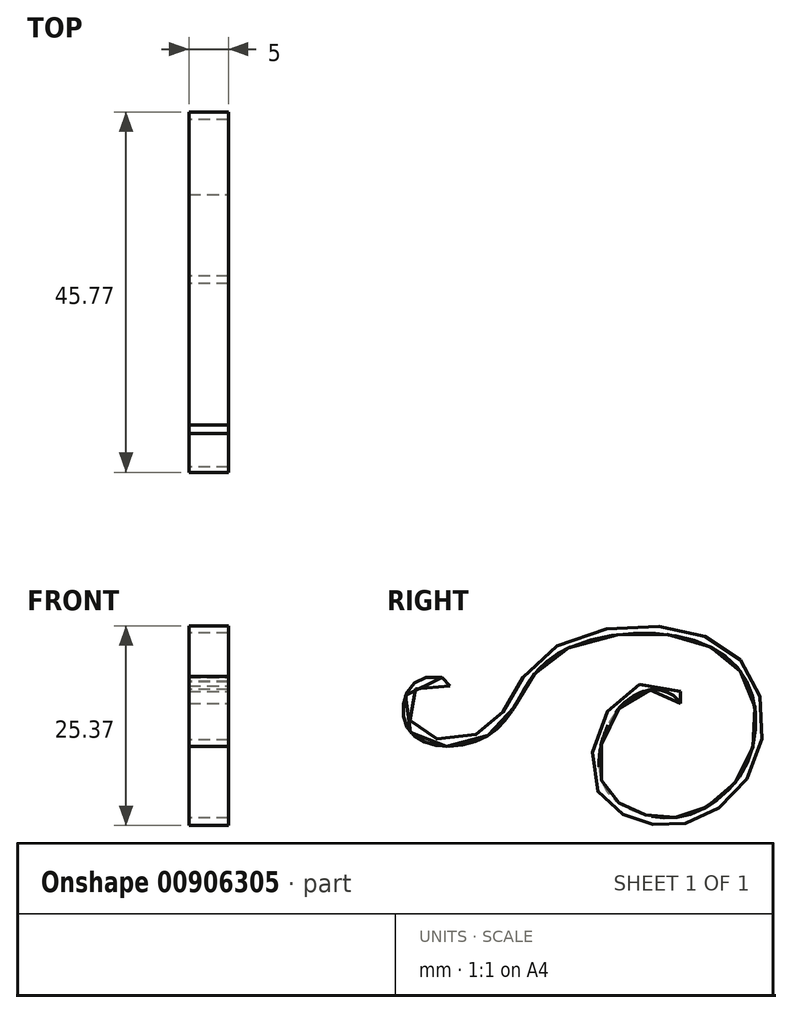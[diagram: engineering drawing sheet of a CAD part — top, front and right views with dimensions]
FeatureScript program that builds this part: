
annotation { "Feature Type Name" : "Feature", "Feature Type Description" : "" }
export const myFeature = defineFeature(function(context is Context, id is Id, definition is map)
    precondition{}
    {
        {
            var Q0;
            Q0=qCreatedBy(makeId("Front.planeOp"),FACE);
            var sketch = newSketch(context, id + "F0", { "sketchPlane" : qUnion([Q0])});
            skLineSegment(sketch, "E0.bottom", {"start": v(-2.5, 0) * mm, "end": v(2.5, 0) * mm});
            skLineSegment(sketch, "E0.top", {"start": v(-2.5, 1.5) * mm, "end": v(2.5, 1.5) * mm});
            skLineSegment(sketch, "E0.left", {"start": v(-2.5, 0) * mm, "end": v(-2.5, 1.5) * mm});
            skLineSegment(sketch, "E0.right", {"start": v(2.5, 0) * mm, "end": v(2.5, 1.5) * mm});
            skSolve(sketch);
        }
        {
            var Q0;
            Q0=qCreatedBy(makeId("Right.planeOp"),FACE);
            var sketch = newSketch(context, id + "F1", { "sketchPlane" : qUnion([Q0])});
            skFitSpline(sketch, "E1", {"points": [v(0, 0) * mm, v(-7.25, 0) * mm, v(-10.1, -9.64) * mm, v(-5.88, -13.7) * mm, v(0.53, -14.3) * mm, v(8.04, -8.38) * mm, v(8.54, 2.48) * mm, v(-1.11, 8.67) * mm, v(-17.4, 5) * mm, v(-24.14, -3.88) * mm, v(-34.6, -3.28) * mm, v(-30.33, 3.3) * mm], "startDerivative": vector(-70.59, 97.6) * mm, "endDerivative": vector(171.98, -30) * mm});
            skSolve(sketch);
        }
        {
            var Q0;
            Q0=makeQuery(id+"F0.imprint","IMPRINT",FACE,{"disambiguationData":[TD([[makeQuery(id+"F0.imprint","IMPRINT",EDGE,{"derivedFrom":sQuery(id+"F0.wireOp",EDGE,"E0.bottom")}),1.0]])]});
            var Q1;
            Q1=sQuery(id+"F1.wireOp",EDGE,"E1");
            sweep(context, id + "F2", {"profiles" : qUnion([Q0]), "path" : qUnion([Q1])});
        }
    });
